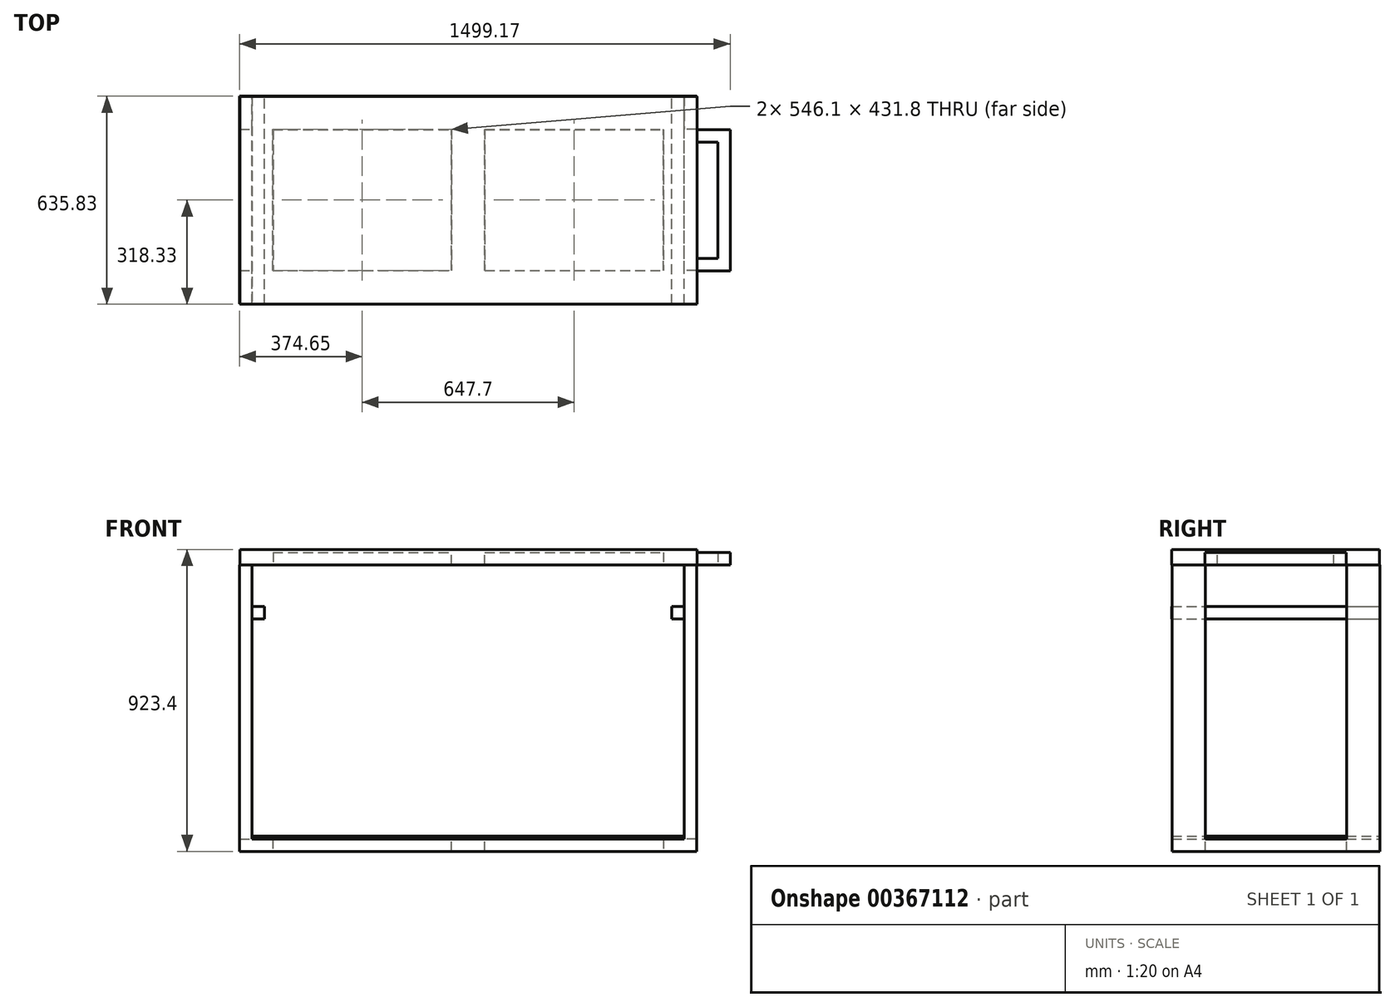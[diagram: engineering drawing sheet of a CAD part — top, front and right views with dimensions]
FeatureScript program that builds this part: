
annotation { "Feature Type Name" : "Feature", "Feature Type Description" : "" }
export const myFeature = defineFeature(function(context is Context, id is Id, definition is map)
    precondition{}
    {
        {
            var Q0;
            Q0=qCreatedBy(makeId("Top.planeOp"),FACE);
            var sketch = newSketch(context, id + "F0", { "sketchPlane" : qUnion([Q0])});
            skLineSegment(sketch, "E0.bottom", {"start": v(-698.5, -317.5) * mm, "end": v(698.5, -317.5) * mm});
            skLineSegment(sketch, "E0.top", {"start": v(-698.5, 317.5) * mm, "end": v(698.5, 317.5) * mm});
            skLineSegment(sketch, "E0.left", {"start": v(-698.5, -317.5) * mm, "end": v(-698.5, 317.5) * mm});
            skLineSegment(sketch, "E0.right", {"start": v(698.5, -317.5) * mm, "end": v(698.5, 317.5) * mm});
            skPoint(sketch, "E0.middle", {"position": v(0, 0) * mm});
            skLineSegment(sketch, "E1.bottom", {"start": v(-596.9, -215.9) * mm, "end": v(596.9, -215.9) * mm});
            skLineSegment(sketch, "E1.top", {"start": v(-596.9, 215.9) * mm, "end": v(596.9, 215.9) * mm});
            skLineSegment(sketch, "E1.left", {"start": v(-596.9, -215.9) * mm, "end": v(-596.9, 215.9) * mm});
            skLineSegment(sketch, "E1.right", {"start": v(596.9, -215.9) * mm, "end": v(596.9, 215.9) * mm});
            skSolve(sketch);
        }
        {
            var Q0;
            Q0=makeQuery(id+"F0.imprint","IMPRINT",FACE,{"disambiguationData":[TD([[makeQuery(id+"F0.imprint","IMPRINT",EDGE,{"derivedFrom":sQuery(id+"F0.wireOp",EDGE,"E0.bottom")}),1.0]])]});
            extrude(context, id + "F1", {"entities" : qUnion([Q0]), "depth" : 38.1 * mm});
        }
        {
            var Q0;
            Q0=makeQuery(id+"F1.opExtrude","CAP_FACE",FACE,{"disambiguationData":[OSD([sQuery(id+"F0.wireOp",EDGE,"E0.bottom"),sQuery(id+"F0.wireOp",EDGE,"E0.top"),sQuery(id+"F0.wireOp",EDGE,"E0.left"),sQuery(id+"F0.wireOp",EDGE,"E0.right"),sQuery(id+"F0.wireOp",EDGE,"E1.bottom"),sQuery(id+"F0.wireOp",EDGE,"E1.top"),sQuery(id+"F0.wireOp",EDGE,"E1.left"),sQuery(id+"F0.wireOp",EDGE,"E1.right")])],"isStart":false});
            var sketch = newSketch(context, id + "F2", { "sketchPlane" : qUnion([Q0])});
            skLineSegment(sketch, "E2.bottom", {"start": v(-698.5, -317.5) * mm, "end": v(-660.4, -317.5) * mm});
            skLineSegment(sketch, "E2.top", {"start": v(-698.5, -215.9) * mm, "end": v(-660.4, -215.9) * mm});
            skLineSegment(sketch, "E2.left", {"start": v(-698.5, -317.5) * mm, "end": v(-698.5, -215.9) * mm});
            skLineSegment(sketch, "E2.right", {"start": v(-660.4, -317.5) * mm, "end": v(-660.4, -215.9) * mm});
            skLineSegment(sketch, "E3.bottom", {"start": v(-698.5, 317.5) * mm, "end": v(-660.4, 317.5) * mm});
            skLineSegment(sketch, "E3.top", {"start": v(-698.5, 215.9) * mm, "end": v(-660.4, 215.9) * mm});
            skLineSegment(sketch, "E3.left", {"start": v(-698.5, 317.5) * mm, "end": v(-698.5, 215.9) * mm});
            skLineSegment(sketch, "E3.right", {"start": v(-660.4, 317.5) * mm, "end": v(-660.4, 215.9) * mm});
            skLineSegment(sketch, "E4.bottom", {"start": v(698.5, 317.5) * mm, "end": v(660.4, 317.5) * mm});
            skLineSegment(sketch, "E4.top", {"start": v(698.5, 215.9) * mm, "end": v(660.4, 215.9) * mm});
            skLineSegment(sketch, "E4.left", {"start": v(698.5, 317.5) * mm, "end": v(698.5, 215.9) * mm});
            skLineSegment(sketch, "E4.right", {"start": v(660.4, 317.5) * mm, "end": v(660.4, 215.9) * mm});
            skLineSegment(sketch, "E5.bottom", {"start": v(698.5, -317.5) * mm, "end": v(660.4, -317.5) * mm});
            skLineSegment(sketch, "E5.top", {"start": v(698.5, -215.9) * mm, "end": v(660.4, -215.9) * mm});
            skLineSegment(sketch, "E5.left", {"start": v(698.5, -317.5) * mm, "end": v(698.5, -215.9) * mm});
            skLineSegment(sketch, "E5.right", {"start": v(660.4, -317.5) * mm, "end": v(660.4, -215.9) * mm});
            skSolve(sketch);
        }
        {
            var Q0;
            Q0 = qSketchRegion(id + "F2", true);
            extrude(context, id + "F3", {"entities" : qUnion([Q0]), "operationType" : NewBodyOperationType.ADD, "depth" : 838.2 * mm});
        }
        {
            var Q0;
            Q0=makeQuery(id+"F3.opExtrude","CAP_FACE",FACE,{"disambiguationData":[OSD([sQuery(id+"F2.wireOp",EDGE,"E3.bottom"),sQuery(id+"F2.wireOp",EDGE,"E3.top"),sQuery(id+"F2.wireOp",EDGE,"E3.left"),sQuery(id+"F2.wireOp",EDGE,"E3.right")])],"isStart":false});
            cPlane(context, id + "F4", {"entities" : qUnion([Q0]), "cplaneType" : CPlaneType.OFFSET, "offset" : 0 * mm, "width" : 152.4 * mm, "height" : 152.4 * mm});
        }
        {
            var Q0;
            Q0=qCreatedBy(id+"F4.planeOp",FACE);
            var sketch = newSketch(context, id + "F5", { "sketchPlane" : qUnion([Q0])});
            skLineSegment(sketch, "E6.bottom", {"start": v(-697.93, 316.67) * mm, "end": v(699.07, 316.67) * mm});
            skLineSegment(sketch, "E6.top", {"start": v(-697.93, -318.33) * mm, "end": v(699.07, -318.33) * mm});
            skLineSegment(sketch, "E6.left", {"start": v(-697.93, 316.67) * mm, "end": v(-697.93, -318.33) * mm});
            skLineSegment(sketch, "E6.right", {"start": v(699.07, 316.67) * mm, "end": v(699.07, -318.33) * mm});
            skLineSegment(sketch, "E7.bottom", {"start": v(-596.33, 215.07) * mm, "end": v(596.33, 215.07) * mm});
            skLineSegment(sketch, "E7.top", {"start": v(-596.33, -215.07) * mm, "end": v(596.33, -215.07) * mm});
            skLineSegment(sketch, "E7.left", {"start": v(-596.33, 215.07) * mm, "end": v(-596.33, -215.07) * mm});
            skLineSegment(sketch, "E7.right", {"start": v(596.33, 215.07) * mm, "end": v(596.33, -215.07) * mm});
            skPoint(sketch, "E7.middle", {"position": v(0, 0) * mm});
            skSolve(sketch);
        }
        {
            var Q0;
            Q0 = qSketchRegion(id + "F5", true);
            extrude(context, id + "F6", {"entities" : qUnion([Q0]), "operationType" : NewBodyOperationType.ADD, "depth" : 38.1 * mm});
        }
        {
            var Q0;
            Q0=makeQuery(id+"F6.opExtrude","SWEPT_FACE",FACE,{"disambiguationData":[OSD([sQuery(id+"F5.wireOp",EDGE,"E7.bottom")])]});
            var sketch = newSketch(context, id + "F7", { "sketchPlane" : qUnion([Q0])});
            skLineSegment(sketch, "E8", {"start": v(0, 914.4) * mm, "end": v(0, 876.3) * mm, "construction": true});
            skLineSegment(sketch, "E9.bottom", {"start": v(-50.8, 876.3) * mm, "end": v(50.8, 876.3) * mm});
            skLineSegment(sketch, "E9.top", {"start": v(-50.8, 914.4) * mm, "end": v(50.8, 914.4) * mm});
            skLineSegment(sketch, "E9.left", {"start": v(-50.8, 876.3) * mm, "end": v(-50.8, 914.4) * mm});
            skLineSegment(sketch, "E9.right", {"start": v(50.8, 876.3) * mm, "end": v(50.8, 914.4) * mm});
            skPoint(sketch, "E9.middle", {"position": v(0, 895.35) * mm});
            skSolve(sketch);
        }
        {
            var Q0;
            Q0=makeQuery(id+"F7.imprint","IMPRINT",FACE,{"disambiguationData":[TD([[makeQuery(id+"F7.imprint","IMPRINT",EDGE,{"derivedFrom":sQuery(id+"F7.wireOp",EDGE,"E9.bottom")}),1.0]])]});
            extrude(context, id + "F8", {"entities" : qUnion([Q0]), "operationType" : NewBodyOperationType.ADD, "depth" : 431.8 * mm});
        }
        {
            var Q0;
            Q0=makeQuery(id+"F1.opExtrude","SWEPT_FACE",FACE,{"disambiguationData":[OSD([sQuery(id+"F0.wireOp",EDGE,"E1.bottom")])]});
            var sketch = newSketch(context, id + "F9", { "sketchPlane" : qUnion([Q0])});
            skLineSegment(sketch, "E10", {"start": v(0, 38.1) * mm, "end": v(0, 0) * mm, "construction": true});
            skLineSegment(sketch, "E11.bottom", {"start": v(50.8, 0) * mm, "end": v(-50.8, 0) * mm});
            skLineSegment(sketch, "E11.top", {"start": v(50.8, 38.1) * mm, "end": v(-50.8, 38.1) * mm});
            skLineSegment(sketch, "E11.left", {"start": v(50.8, 0) * mm, "end": v(50.8, 38.1) * mm});
            skLineSegment(sketch, "E11.right", {"start": v(-50.8, 0) * mm, "end": v(-50.8, 38.1) * mm});
            skPoint(sketch, "E11.middle", {"position": v(0, 19.05) * mm});
            skSolve(sketch);
        }
        {
            var Q0;
            Q0=makeQuery(id+"F9.imprint","IMPRINT",FACE,{"disambiguationData":[TD([[makeQuery(id+"F9.imprint","IMPRINT",EDGE,{"derivedFrom":sQuery(id+"F9.wireOp",EDGE,"E11.bottom")}),-1.0]])]});
            extrude(context, id + "F10", {"entities" : qUnion([Q0]), "operationType" : NewBodyOperationType.ADD, "depth" : 431.8 * mm});
        }
        {
            var Q0;
            Q0=makeQuery(id+"F6.opExtrude","SWEPT_FACE",FACE,{"disambiguationData":[OSD([sQuery(id+"F5.wireOp",EDGE,"E6.right")])]});
            var sketch = newSketch(context, id + "F11", { "sketchPlane" : qUnion([Q0])});
            skLineSegment(sketch, "E12.bottom", {"start": v(-216.73, 876.3) * mm, "end": v(-178.63, 876.3) * mm});
            skLineSegment(sketch, "E12.top", {"start": v(-216.73, 914.4) * mm, "end": v(-178.63, 914.4) * mm});
            skLineSegment(sketch, "E12.left", {"start": v(-216.73, 876.3) * mm, "end": v(-216.73, 914.4) * mm});
            skLineSegment(sketch, "E12.right", {"start": v(-178.63, 876.3) * mm, "end": v(-178.63, 914.4) * mm});
            skLineSegment(sketch, "E13.bottom", {"start": v(215.07, 876.3) * mm, "end": v(176.97, 876.3) * mm});
            skLineSegment(sketch, "E13.top", {"start": v(215.07, 914.4) * mm, "end": v(176.97, 914.4) * mm});
            skLineSegment(sketch, "E13.left", {"start": v(215.07, 876.3) * mm, "end": v(215.07, 914.4) * mm});
            skLineSegment(sketch, "E13.right", {"start": v(176.97, 876.3) * mm, "end": v(176.97, 914.4) * mm});
            skSolve(sketch);
        }
        {
            var Q0;
            Q0 = qSketchRegion(id + "F11", true);
            extrude(context, id + "F12", {"entities" : qUnion([Q0]), "operationType" : NewBodyOperationType.ADD, "depth" : 101.6 * mm});
        }
        {
            var Q0;
            Q0=makeQuery(id+"F12.opExtrude","SWEPT_FACE",FACE,{"disambiguationData":[OSD([sQuery(id+"F11.wireOp",EDGE,"E12.right")])]});
            var sketch = newSketch(context, id + "F13", { "sketchPlane" : qUnion([Q0])});
            skLineSegment(sketch, "E14.bottom", {"start": v(-800.67, 914.4) * mm, "end": v(-762.57, 914.4) * mm});
            skLineSegment(sketch, "E14.top", {"start": v(-800.67, 876.3) * mm, "end": v(-762.57, 876.3) * mm});
            skLineSegment(sketch, "E14.left", {"start": v(-800.67, 914.4) * mm, "end": v(-800.67, 876.3) * mm});
            skLineSegment(sketch, "E14.right", {"start": v(-762.57, 914.4) * mm, "end": v(-762.57, 876.3) * mm});
            skSolve(sketch);
        }
        {
            var Q0;
            Q0 = qSketchRegion(id + "F13", true);
            extrude(context, id + "F14", {"entities" : qUnion([Q0]), "operationType" : NewBodyOperationType.ADD, "depth" : 358.14 * mm});
        }
        {
            var Q0;
            Q0=makeQuery(id+"F6.opExtrude","SWEPT_FACE",FACE,{"disambiguationData":[OSD([sQuery(id+"F5.wireOp",EDGE,"E6.bottom")])]});
            var sketch = newSketch(context, id + "F15", { "sketchPlane" : qUnion([Q0])});
            skLineSegment(sketch, "E15", {"start": v(660.4, 914.4) * mm, "end": v(660.4, 749.3) * mm, "construction": true});
            skLineSegment(sketch, "E16", {"start": v(-660.4, 914.4) * mm, "end": v(-660.4, 749.3) * mm, "construction": true});
            skLineSegment(sketch, "E17.bottom", {"start": v(-660.4, 749.3) * mm, "end": v(-622.3, 749.3) * mm});
            skLineSegment(sketch, "E17.top", {"start": v(-660.4, 711.2) * mm, "end": v(-622.3, 711.2) * mm});
            skLineSegment(sketch, "E17.left", {"start": v(-660.4, 749.3) * mm, "end": v(-660.4, 711.2) * mm});
            skLineSegment(sketch, "E17.right", {"start": v(-622.3, 749.3) * mm, "end": v(-622.3, 711.2) * mm});
            skLineSegment(sketch, "E18.bottom", {"start": v(660.4, 749.3) * mm, "end": v(622.3, 749.3) * mm});
            skLineSegment(sketch, "E18.top", {"start": v(660.4, 711.2) * mm, "end": v(622.3, 711.2) * mm});
            skLineSegment(sketch, "E18.left", {"start": v(660.4, 749.3) * mm, "end": v(660.4, 711.2) * mm});
            skLineSegment(sketch, "E18.right", {"start": v(622.3, 749.3) * mm, "end": v(622.3, 711.2) * mm});
            skSolve(sketch);
        }
        {
            var Q0;
            Q0 = qSketchRegion(id + "F15", true);
            extrude(context, id + "F16", {"entities" : qUnion([Q0]), "operationType" : NewBodyOperationType.ADD, "oppositeDirection" : true, "depth" : 635 * mm});
        }
        {
            var Q0;
            Q0=makeQuery(id+"F10.boolean.opBoolean","MERGE",FACE,{"derivedFrom":[makeQuery(id+"F1.opExtrude","CAP_FACE",FACE,{"disambiguationData":[OSD([sQuery(id+"F0.wireOp",EDGE,"E0.bottom"),sQuery(id+"F0.wireOp",EDGE,"E0.top"),sQuery(id+"F0.wireOp",EDGE,"E0.left"),sQuery(id+"F0.wireOp",EDGE,"E0.right"),sQuery(id+"F0.wireOp",EDGE,"E1.bottom"),sQuery(id+"F0.wireOp",EDGE,"E1.top"),sQuery(id+"F0.wireOp",EDGE,"E1.left"),sQuery(id+"F0.wireOp",EDGE,"E1.right")])],"isStart":false}),makeQuery(id+"F10.opExtrude","SWEPT_FACE",FACE,{"disambiguationData":[OSD([sQuery(id+"F9.wireOp",EDGE,"E11.top")])]})]});
            var sketch = newSketch(context, id + "F17", { "sketchPlane" : qUnion([Q0])});
            skLineSegment(sketch, "E19.bottom", {"start": v(660.4, -317.5) * mm, "end": v(-660.4, -317.5) * mm});
            skLineSegment(sketch, "E19.top", {"start": v(660.4, 317.5) * mm, "end": v(-660.4, 317.5) * mm});
            skLineSegment(sketch, "E19.left", {"start": v(660.4, -317.5) * mm, "end": v(660.4, 317.5) * mm});
            skLineSegment(sketch, "E19.right", {"start": v(-660.4, -317.5) * mm, "end": v(-660.4, 317.5) * mm});
            skSolve(sketch);
        }
        {
            var Q0;
            Q0 = qSketchRegion(id + "F17", true);
            extrude(context, id + "F18", {"entities" : qUnion([Q0]), "depth" : 9 * mm});
        }
        {
            var Q0;
            Q0=makeQuery(id+"F14.boolean.opBoolean","MERGE",FACE,{"derivedFrom":[makeQuery(id+"F12.boolean.opBoolean","MERGE",FACE,{"derivedFrom":[makeQuery(id+"F8.boolean.opBoolean","MERGE",FACE,{"derivedFrom":[makeQuery(id+"F6.opExtrude","CAP_FACE",FACE,{"disambiguationData":[OSD([sQuery(id+"F5.wireOp",EDGE,"E6.bottom"),sQuery(id+"F5.wireOp",EDGE,"E6.top"),sQuery(id+"F5.wireOp",EDGE,"E6.left"),sQuery(id+"F5.wireOp",EDGE,"E6.right"),sQuery(id+"F5.wireOp",EDGE,"E7.bottom"),sQuery(id+"F5.wireOp",EDGE,"E7.top"),sQuery(id+"F5.wireOp",EDGE,"E7.left"),sQuery(id+"F5.wireOp",EDGE,"E7.right")])],"isStart":false}),makeQuery(id+"F8.opExtrude","SWEPT_FACE",FACE,{"disambiguationData":[OSD([sQuery(id+"F7.wireOp",EDGE,"E9.top")])]})]}),makeQuery(id+"F12.opExtrude","SWEPT_FACE",FACE,{"disambiguationData":[OSD([sQuery(id+"F11.wireOp",EDGE,"E12.top")])]}),makeQuery(id+"F12.opExtrude","SWEPT_FACE",FACE,{"disambiguationData":[OSD([sQuery(id+"F11.wireOp",EDGE,"E13.top")])]})]}),makeQuery(id+"F14.opExtrude","SWEPT_FACE",FACE,{"disambiguationData":[OSD([sQuery(id+"F13.wireOp",EDGE,"E14.bottom")])]})]});
            var sketch = newSketch(context, id + "F19", { "sketchPlane" : qUnion([Q0])});
            skLineSegment(sketch, "E20.bottom", {"start": v(699.07, -318.33) * mm, "end": v(-697.93, -318.33) * mm});
            skLineSegment(sketch, "E20.top", {"start": v(699.07, 316.67) * mm, "end": v(-697.93, 316.67) * mm});
            skLineSegment(sketch, "E20.left", {"start": v(699.07, -318.33) * mm, "end": v(699.07, 316.67) * mm});
            skLineSegment(sketch, "E20.right", {"start": v(-697.93, -318.33) * mm, "end": v(-697.93, 316.67) * mm});
            skSolve(sketch);
        }
        {
            var Q0;
            Q0 = qSketchRegion(id + "F19", true);
            extrude(context, id + "F20", {"entities" : qUnion([Q0]), "depth" : 9 * mm});
        }
        {
            var Q0;
            Q0=makeQuery(id+"F18.opExtrude","CAP_FACE",FACE,{"disambiguationData":[OSD([sQuery(id+"F17.wireOp",EDGE,"E19.bottom"),sQuery(id+"F17.wireOp",EDGE,"E19.top"),sQuery(id+"F17.wireOp",EDGE,"E19.left"),sQuery(id+"F17.wireOp",EDGE,"E19.right")])],"isStart":false});
            var sketch = newSketch(context, id + "F21", { "sketchPlane" : qUnion([Q0])});
            skCircle(sketch, "E21", {"center": v(-688.4, 307.98) * mm, "radius": 3.18 * mm});
            skCircle(sketch, "E22", {"center": v(689.55, -308.8) * mm, "radius": 3.18 * mm});
            skSolve(sketch);
        }
        {
            var Q0;
            Q0 = qSketchRegion(id + "F21", true);
            extrude(context, id + "F22", {"entities" : qUnion([Q0]), "operationType" : NewBodyOperationType.ADD, "depth" : 876.05 * mm});
        }
    });
